# Revit family: 2. Вентиляторы KORF ANR V1 REZ
name_source: partatom
category: Оборудование
revit_build: Autodesk Revit 2016 (Build: 20151209_0715(x64)
units: mm (PartAtom-declared; Revit-internal decimal feet)

## family parameters
Всегда вертикально = Да
На основе рабочей плоскости = Нет
Общий = Нет
При загрузке вырезать с полостями = Нет
Размер круглого соединителя = Использовать диаметр
Тип детали = Нормальный
Точка расчета площади = Нет

## types (26) — shared parameters
h = 130 мм
Единица измерения = шт.
Завод изготовитель = KORF
Ключевая пометка = Вентиляция
Раздел = ОВ
Синий = Синий
высота ножек = 120 мм

## per-type parameters (varying)
| type | А | А1 | Б | Б1 | Высота | Д | Д1 | Материал | Наименование и тех.хар-ка | Середина | Тип, марка, обозначение | Ширина |
| ANR 6 V1.0. | 1100 мм | 1080 мм | 1100 мм | 1080 мм | 1025 мм | 1100 мм | 1080 мм | Сталь серая | Секция вентилятора с резервным двигателем короткая с назад загнутыми лопатками и выбросом прямо | 670 мм | ANR 6 V1.0. REZ | 1025 мм |
| ANR 7 V1.0. | 1100 мм | 1080 мм | 1320 мм | 1300 мм | 1245 мм | 1100 мм | 1080 мм | Сталь серая | Секция вентилятора с резервным двигателем короткая с назад загнутыми лопатками и выбросом прямо | 780 мм | ANR 7 V1.0. REZ | 1025 мм |
| ANR 8 V1.0. | 1320 мм | 1300 мм | 1320 мм | 1300 мм | 1245 мм | 1100 мм | 1080 мм | Сталь серая | Секция вентилятора с резервным двигателем короткая с назад загнутыми лопатками и выбросом прямо | 780 мм | ANR 8 V1.0. REZ | 1025 мм |
| ANR 12 V1.0. | 1435 мм | 1415 мм | 1435 мм | 1415 мм | 1360 мм | 1100 мм | 1080 мм | Сталь серая | Секция вентилятора с резервным двигателем короткая с назад загнутыми лопатками и выбросом прямо | 838 мм | ANR 12 V1.0. REZ | 1025 мм |
| ANR 20 V1.0. | 1660 мм | 1640 мм | 1660 мм | 1640 мм | 1585 мм | 1100 мм | 1080 мм | Сталь серая | Секция вентилятора с резервным двигателем короткая с назад загнутыми лопатками и выбросом прямо | 950 мм | ANR 20 V1.0. REZ | 1025 мм |
| ANR 25 V1.0. | 2045 мм | 2025 мм | 2045 мм | 2025 мм | 1970 мм | 1100 мм | 1080 мм | Сталь серая | Секция вентилятора с резервным двигателем короткая с назад загнутыми лопатками и выбросом прямо | 1143 мм | ANR 25 V1.0. REZ | 1025 мм |
| ANR 30 V1.1. | 2485 мм | 2465 мм | 2045 мм | 2025 мм | 1970 мм | 1625 мм | 1605 мм | Сталь серая | Секция вентилятора с резервным двигателем удлиненная с назад загнутыми лопатками и выбросом прямо | 1143 мм | ANR 30 V1.1. REZ | 1550 мм |
| ANR 35 V1.1. | 2485 мм | 2465 мм | 2485 мм | 2465 мм | 2410 мм | 1625 мм | 1605 мм | Сталь серая | Секция вентилятора с резервным двигателем удлиненная с назад загнутыми лопатками и выбросом прямо | 1363 мм | ANR 35 V1.1. REZ | 1550 мм |
| ANR 40 V1.1. | 3320 мм | 3300 мм | 3320 мм | 3300 мм | 3245 мм | 1625 мм | 1605 мм | Сталь серая | Секция вентилятора с резервным двигателем удлиненная с назад загнутыми лопатками и выбросом прямо | 1780 мм | ANR 40 V1.1. REZ | 1550 мм |
| ANR 45 V1.1. | 3320 мм | 3300 мм | 4090 мм | 4070 мм | 4015 мм | 1625 мм | 1605 мм | Сталь серая | Секция вентилятора с резервным двигателем удлиненная с назад загнутыми лопатками и выбросом прямо | 2165 мм | ANR 45 V1.1. REZ | 1550 мм |
| ANR 6 V1.1. | 1100 мм | 1080 мм | 1100 мм | 1080 мм | 1025 мм | 1625 мм | 1605 мм | Сталь серая | Секция вентилятора с резервным двигателем удлиненная с назад загнутыми лопатками и выбросом прямо | 670 мм | ANR 6 V1.1. REZ | 1550 мм |
| ANR 6 V1.2. | 1100 мм | 1080 мм | 1100 мм | 1080 мм | 1025 мм | 1625 мм | 1605 мм | Сталь серая | Секция вентилятора с резервным двигателем длинная с назад загнутыми лопатками и выбросом прямо | 670 мм | ANR 6 V1.1. REZ | 1550 мм |
| ANR 7 V1.1. | 1100 мм | 1080 мм | 1320 мм | 1300 мм | 1245 мм | 1625 мм | 1605 мм | Сталь серая | Секция вентилятора с резервным двигателем удлиненная с назад загнутыми лопатками и выбросом прямо | 780 мм | ANR 7 V1.1. REZ | 1550 мм |
| ANR 7 V1.2. | 1100 мм | 1080 мм | 1320 мм | 1300 мм | 1245 мм | 1625 мм | 1605 мм | Сталь серая | Секция вентилятора с резервным двигателем длинная с назад загнутыми лопатками и выбросом прямо | 780 мм | ANR 7 V1.2. REZ | 1550 мм |
| ANR 8 V1.1. | 1320 мм | 1300 мм | 1320 мм | 1300 мм | 1245 мм | 1625 мм | 1605 мм | Сталь серая | Секция вентилятора с резервным двигателем удлиненная с назад загнутыми лопатками и выбросом прямо | 780 мм | ANR 8 V1.1. REZ | 1550 мм |
| ANR 8 V1.2. | 1320 мм | 1300 мм | 1320 мм | 1300 мм | 1245 мм | 1625 мм | 1605 мм | RAL 0000 Серый металл | Секция вентилятора с резервным двигателем длинная с назад загнутыми лопатками и выбросом прямо | 780 мм | ANR 8 V1.2. REZ | 1550 мм |
| ANR 12 V1.1. | 1435 мм | 1415 мм | 1435 мм | 1415 мм | 1360 мм | 1625 мм | 1605 мм | Сталь серая | Секция вентилятора с резервным двигателем удлиненная с назад загнутыми лопатками и выбросом прямо | 838 мм | ANR 12 V1.1. REZ | 1550 мм |
| ANR 12 V1.2. | 1435 мм | 1415 мм | 1435 мм | 1415 мм | 1360 мм | 1625 мм | 1605 мм | Сталь серая | Секция вентилятора с резервным двигателем длинная с назад загнутыми лопатками и выбросом прямо | 838 мм | ANR 12 V1.2. REZ | 1550 мм |
| ANR 20 V1.1. | 1660 мм | 1640 мм | 1660 мм | 1640 мм | 1585 мм | 1625 мм | 1605 мм | Сталь серая | Секция вентилятора с резервным двигателем удлиненная с назад загнутыми лопатками и выбросом прямо | 950 мм | ANR 20 V1.1. REZ | 1550 мм |
| ANR 20 V1.2. | 1660 мм | 1640 мм | 1660 мм | 1640 мм | 1585 мм | 1625 мм | 1605 мм | Сталь серая | Секция вентилятора с резервным двигателем длинная с назад загнутыми лопатками и выбросом прямо | 950 мм | ANR 20 V1.2. REZ | 1550 мм |
| ANR 25 V1.1. | 2045 мм | 2025 мм | 2045 мм | 2025 мм | 1970 мм | 1625 мм | 1605 мм | Сталь серая | Секция вентилятора с резервным двигателем удлиненная с назад загнутыми лопатками и выбросом прямо | 1143 мм | ANR 25 V1.1. REZ | 1550 мм |
| ANR 25 V1.2. | 2045 мм | 2025 мм | 2045 мм | 2025 мм | 1970 мм | 1625 мм | 1605 мм | Сталь серая | Секция вентилятора с резервным двигателем длинная с назад загнутыми лопатками и выбросом прямо | 1143 мм | ANR 25 V1.2. REZ | 1550 мм |
| ANR 30 V1.2. | 2485 мм | 2465 мм | 2045 мм | 2025 мм | 1970 мм | 1625 мм | 1605 мм | Сталь серая | Секция вентилятора с резервным двигателем длинная с назад загнутыми лопатками и выбросом прямо | 1143 мм | ANR 30 V1.2. REZ | 1550 мм |
| ANR 35 V1.2. | 2485 мм | 2465 мм | 2485 мм | 2465 мм | 2410 мм | 1625 мм | 1605 мм | Сталь серая | Секция вентилятора с резервным двигателем длинная с назад загнутыми лопатками и выбросом прямо | 1363 мм | ANR 35 V1.2. REZ | 1550 мм |
| ANR 40 V1.2. | 3320 мм | 3300 мм | 3320 мм | 3300 мм | 3245 мм | 1625 мм | 1605 мм | Сталь серая | Секция вентилятора с резервным двигателем длинная с назад загнутыми лопатками и выбросом прямо | 1780 мм | ANR 40 V1.2. REZ | 1550 мм |
| ANR 45 V1.2. | 3320 мм | 3300 мм | 4090 мм | 4070 мм | 4015 мм | 1625 мм | 1605 мм | Сталь серая | Секция вентилятора с резервным двигателем длинная с назад загнутыми лопатками и выбросом прямо | 2165 мм | ANR 45 V1.2. REZ | 1550 мм |
